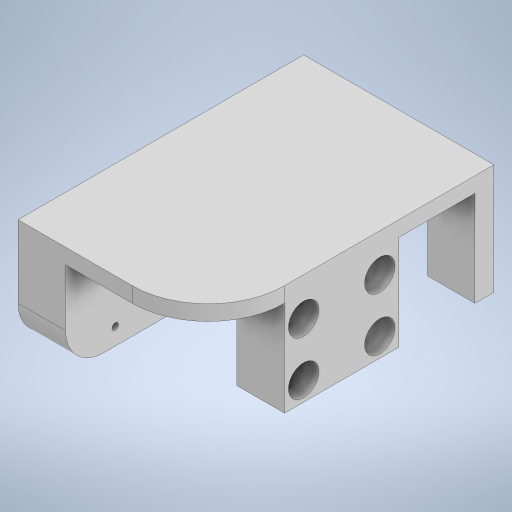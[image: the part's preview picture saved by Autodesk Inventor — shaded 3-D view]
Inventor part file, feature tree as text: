
AUTODESK INVENTOR PART (.ipt)
format: ipt  version: 2024.1 (Build 281209000, 209)  size: 339,968 bytes
history: native  units: mm
features: extrude x8, sketch x8, fillet x2, other x1
ambient origin geometry x8: Origin, YZ Plane, XZ Plane, XY Plane, X Axis, Y Axis, Z Axis, Center Point
bodies: Body1 (feature_tree)
feature tree (19):
  other  "ソリッド1"
  extrude  "押し出し1"  Depth=50.0mm
  extrude  "押し出し2"  Depth=75.0mm
  extrude  "押し出し3"  Depth=29.0mm TaperAngle=0.0deg
  extrude  "押し出し4"  Depth=25.0mm
  extrude  "押し出し5"  Depth=25.0mm TaperAngle=0.0deg
  fillet  "フィレット1"  Radius=20.0mm
  extrude  "押し出し6"  Depth=20.0mm
  fillet  "フィレット2"  Radius=50.0mm
  extrude  "押し出し7"  Depth=29.0mm TaperAngle=0.0deg
  extrude  "押し出し8"  Depth=1.7mm
  sketch  "スケッチ1"
  sketch  "スケッチ2"
  sketch  "スケッチ3"
  sketch  "スケッチ4"
  sketch  "スケッチ5"
  sketch  "スケッチ7"
  sketch  "スケッチ8"
  sketch  "スケッチ9"
